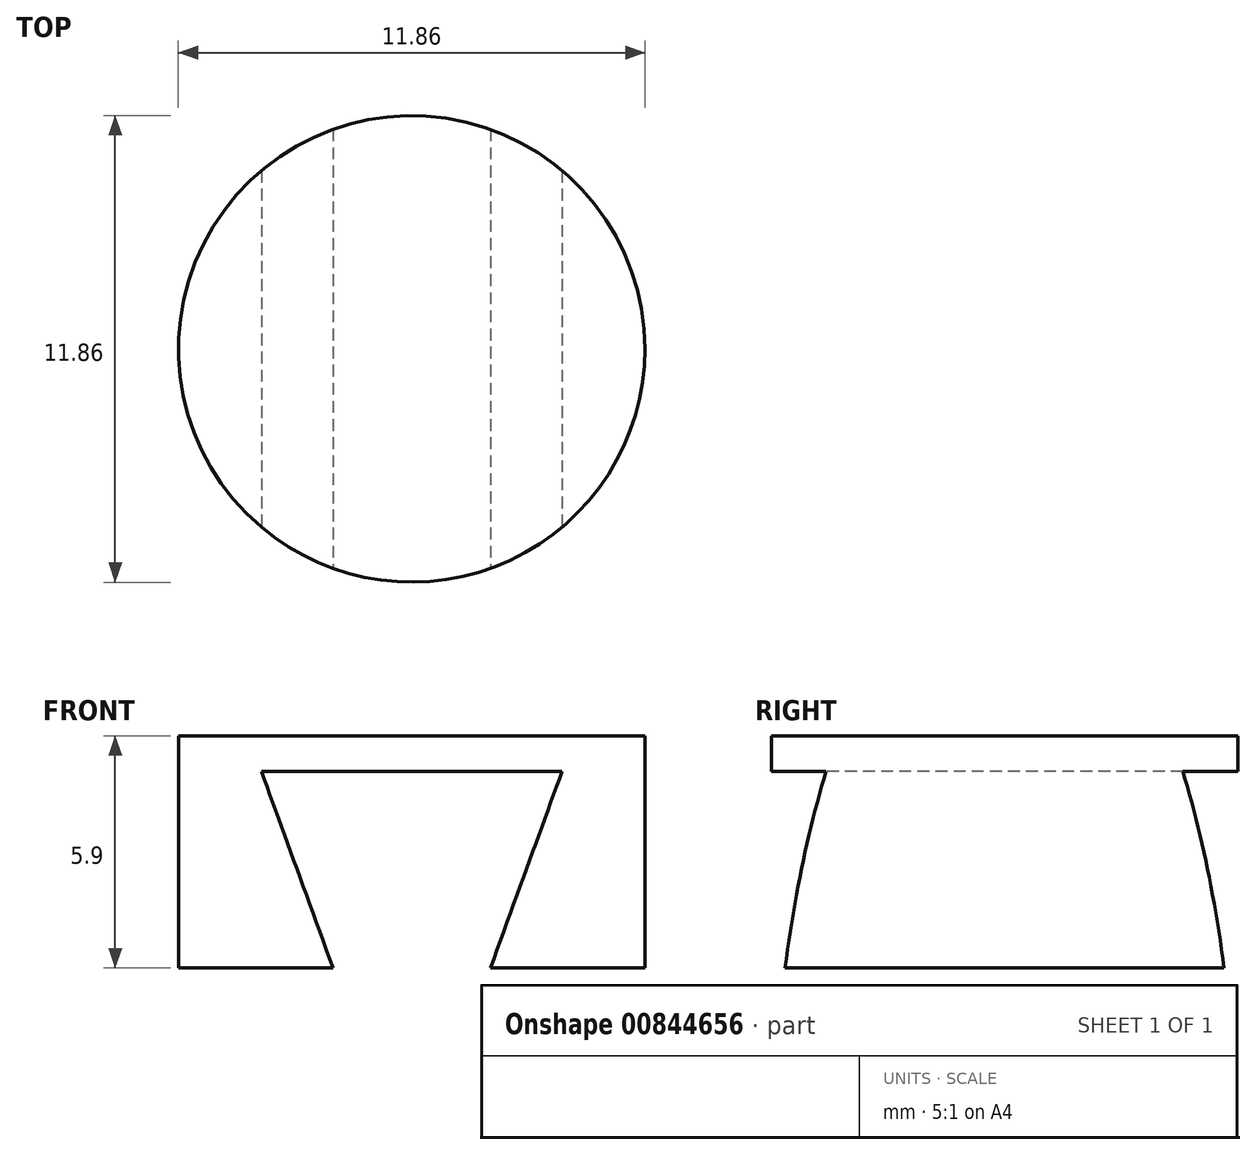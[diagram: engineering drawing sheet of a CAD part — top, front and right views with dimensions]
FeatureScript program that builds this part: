
annotation { "Feature Type Name" : "Feature", "Feature Type Description" : "" }
export const myFeature = defineFeature(function(context is Context, id is Id, definition is map)
    precondition{}
    {
        {
            var Q0;
            Q0=qCreatedBy(makeId("Top.planeOp"),FACE);
            var sketch = newSketch(context, id + "F0", { "sketchPlane" : qUnion([Q0])});
            skCircle(sketch, "E0", {"center": v(0, 0) * mm, "radius": 5.93 * mm});
            skSolve(sketch);
        }
        {
            var Q0;
            Q0 = qSketchRegion(id + "F0", true);
            extrude(context, id + "F1", {"entities" : qUnion([Q0]), "depth" : 5.9 * mm, "offsetDistance" : 25 * mm});
        }
        {
            var Q0;
            Q0=qCreatedBy(makeId("Front.planeOp"),FACE);
            var sketch = newSketch(context, id + "F2", { "sketchPlane" : qUnion([Q0])});
            skLineSegment(sketch, "E1", {"start": v(0, 0) * mm, "end": v(2, 0) * mm});
            skLineSegment(sketch, "E2", {"start": v(2, 0) * mm, "end": v(0, 0) * mm});
            skLineSegment(sketch, "E3", {"start": v(0, 0) * mm, "end": v(-2, 0) * mm});
            skLineSegment(sketch, "E4", {"start": v(2, 0) * mm, "end": v(3.82, 5) * mm});
            skLineSegment(sketch, "E5", {"start": v(3.82, 5) * mm, "end": v(-3.82, 5) * mm});
            skLineSegment(sketch, "E6", {"start": v(-3.82, 5) * mm, "end": v(-2, 0) * mm});
            skSolve(sketch);
        }
        {
            var Q0;
            Q0 = qSketchRegion(id + "F2", true);
            extrude(context, id + "F3", {"entities" : qUnion([Q0]), "operationType" : NewBodyOperationType.REMOVE, "endBound" : BoundingType.SYMMETRIC, "oppositeDirection" : true, "depth" : 25 * mm, "offsetDistance" : 25 * mm});
        }
    });
